# Revit family: NEW
name_source: partatom
category: Plumbing Fixtures
revit_build: Autodesk Revit 2018 (Build: 20170223_1515(x64)
units: mm (PartAtom-declared; Revit-internal decimal feet)

## family parameters
Always vertical = No
Cut with Voids When Loaded = No
OmniClass Number = 23.31.17.00
Part Type = Normal
Room Calculation Point = No
Round Connector Dimension = Use Diameter
Shared = No
Work Plane-Based = No

## types (5) — shared parameters
Always visible = Yes
BIMobject category = Showers
Design country = Germany
EAN code = 4059625203002
Edition number = 1
GTIN code = https://4059625203002
IFC Classification = Sanitary Terminal
Installation instructions = https://www.hansgrohe.com
Manufacturer country = Germany
Manufacturer name = hansgrohe
Material 1 = Hansgrohe - Finoris - Black
Material 3 = Hansgrohe - Finoris - White
Material main = Chrome
Material secondary = Chrome
OmniClass Code = 23-31 17 00
OmniClass Description = Showers
Product Guid = ad0c3983-c753-4127-b44f-534a79eb1b9b
Product SKU = 28020XXX
Product data url = https://www.bimobject.com
Product family = sBox
Product group = Concealed Basic set bath/shower mixers
Product name = 28020XXX sBox Finish set oval
Product url = https://www.hansgrohe.com
QR code = https://www.bimobject.com
Technical description = https://www.hansgrohe.com
Uniclass 1.4 Code = L7214
Uniclass 1.4 Description = Showers
Uniclass 2015 Code = SL_35_80_80
Uniclass 2015 Name = Showers
Weight Net (Kg) = 2,8

## per-type parameters (varying)
| type | Material 2 |
| 990 Polished Gold Optic | Hansgrohe - Finoris - 990 Polished Gold Optic |
| 700 Matt White | Hansgrohe - Finoris - 700 Matt White |
| 670 Matte Black | Hansgrohe - Finoris - 670 Matte Black |
| 340 Brushed Black Chrome | Hansgrohe - Finoris - 340 Brushed Black Chrome |
| 140 Brushed Bronze | Hansgrohe - Finoris - 140 Brushed Bronze |

## geometry (parser evidence)
native form markers: Sweep x2
no freeform markers — native parametric forms only
